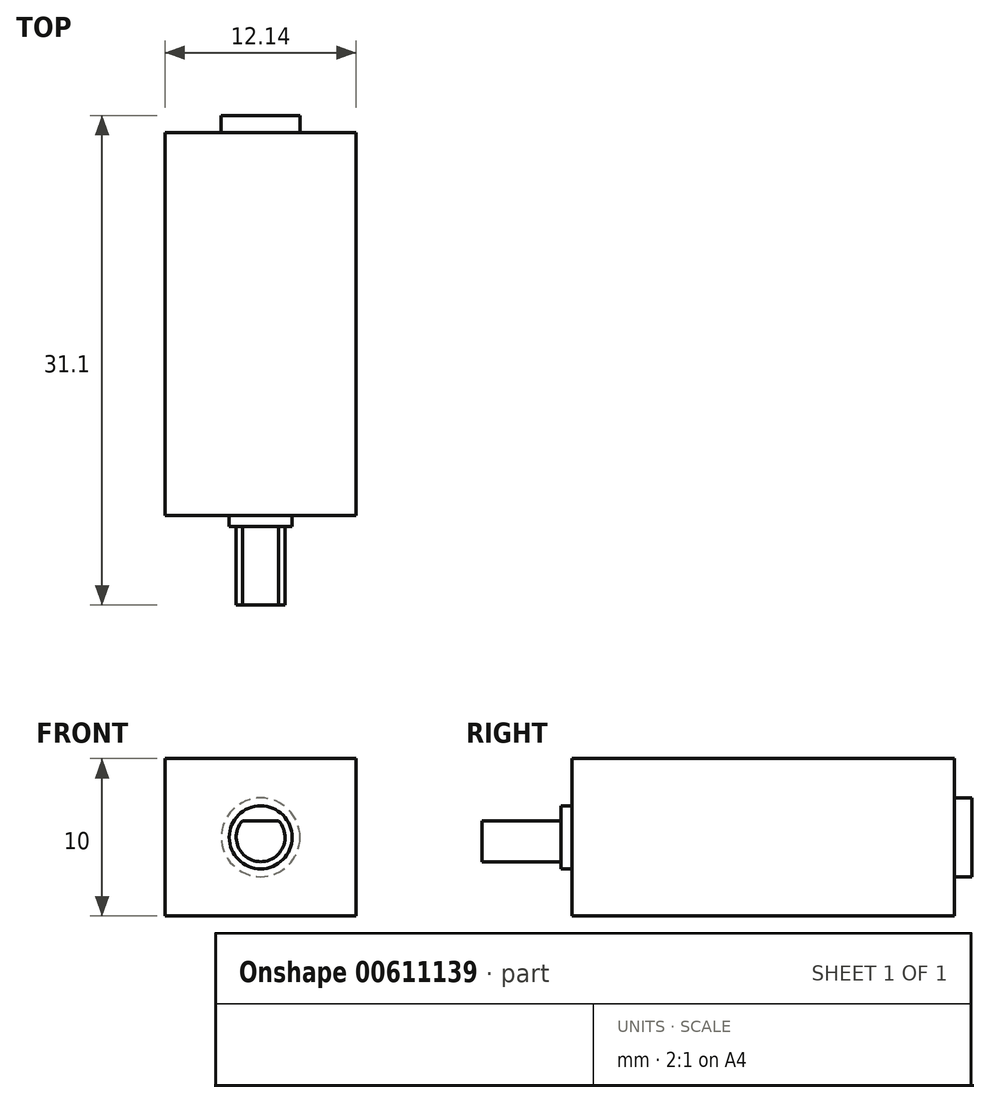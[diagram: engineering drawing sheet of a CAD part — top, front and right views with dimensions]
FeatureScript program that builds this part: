
annotation { "Feature Type Name" : "Feature", "Feature Type Description" : "" }
export const myFeature = defineFeature(function(context is Context, id is Id, definition is map)
    precondition{}
    {
        {
            var Q0;
            Q0=qCreatedBy(makeId("Top.planeOp"),FACE);
            var sketch = newSketch(context, id + "F0", { "sketchPlane" : qUnion([Q0])});
            skLineSegment(sketch, "E0.bottom", {"start": v(-55.86, 44.9) * mm, "end": v(-43.72, 44.9) * mm});
            skLineSegment(sketch, "E0.top", {"start": v(-55.86, 20.6) * mm, "end": v(-43.72, 20.6) * mm});
            skLineSegment(sketch, "E0.left", {"start": v(-55.86, 44.9) * mm, "end": v(-55.86, 20.6) * mm});
            skLineSegment(sketch, "E0.right", {"start": v(-43.72, 44.9) * mm, "end": v(-43.72, 20.6) * mm});
            skSolve(sketch);
        }
        {
            var Q0;
            Q0=makeQuery(id+"F0.imprint","IMPRINT",FACE,{"disambiguationData":[TD([[makeQuery(id+"F0.imprint","IMPRINT",EDGE,{"derivedFrom":sQuery(id+"F0.wireOp",EDGE,"E0.bottom")}),-1.0]])]});
            extrude(context, id + "F1", {"entities" : qUnion([Q0]), "depth" : 10 * mm, "offsetDistance" : 25 * mm});
        }
        {
            var Q0;
            Q0=makeQuery(id+"F1.opExtrude","SWEPT_FACE",FACE,{"disambiguationData":[OSD([sQuery(id+"F0.wireOp",EDGE,"E0.bottom")])]});
            var sketch = newSketch(context, id + "F2", { "sketchPlane" : qUnion([Q0])});
            skCircle(sketch, "E1", {"center": v(49.8, 5) * mm, "radius": 2.5 * mm});
            skSolve(sketch);
        }
        {
            var Q0;
            Q0=makeQuery(id+"F2.imprint","IMPRINT",FACE,{"disambiguationData":[TD([[makeQuery(id+"F2.imprint","IMPRINT",EDGE,{"derivedFrom":sQuery(id+"F2.wireOp",EDGE,"E1")}),1.0]])]});
            var Q1;
            Q1=sQuery(id+"F2.wireOp",EDGE,"E1");
            extrude(context, id + "F3", {"entities" : qUnion([Q0]), "operationType" : NewBodyOperationType.ADD, "surfaceEntities" : qUnion([Q1]), "depth" : 1.1 * mm, "offsetDistance" : 25 * mm});
        }
        {
            var Q0;
            Q0=makeQuery(id+"F1.opExtrude","SWEPT_FACE",FACE,{"disambiguationData":[OSD([sQuery(id+"F0.wireOp",EDGE,"E0.top")])]});
            var sketch = newSketch(context, id + "F4", { "sketchPlane" : qUnion([Q0])});
            skCircle(sketch, "E2", {"center": v(-49.8, 5) * mm, "radius": 2 * mm});
            skSolve(sketch);
        }
        {
            var Q0;
            Q0=makeQuery(id+"F4.imprint","IMPRINT",FACE,{"disambiguationData":[TD([[makeQuery(id+"F4.imprint","IMPRINT",EDGE,{"derivedFrom":sQuery(id+"F4.wireOp",EDGE,"E2")}),1.0]])]});
            var Q1;
            Q1=sQuery(id+"F4.wireOp",EDGE,"E2");
            extrude(context, id + "F5", {"entities" : qUnion([Q0]), "operationType" : NewBodyOperationType.ADD, "surfaceEntities" : qUnion([Q1]), "depth" : 0.7 * mm, "offsetDistance" : 25 * mm});
        }
        {
            var Q0;
            Q0=makeQuery(id+"F5.opExtrude","CAP_FACE",FACE,{"disambiguationData":[OSD([sQuery(id+"F4.wireOp",EDGE,"E2")])],"isStart":false});
            var sketch = newSketch(context, id + "F6", { "sketchPlane" : qUnion([Q0])});
            skCircle(sketch, "E3", {"center": v(-49.8, 5) * mm, "radius": 1.55 * mm});
            skLineSegment(sketch, "E4", {"start": v(-50.93, 6.05) * mm, "end": v(-48.65, 6.05) * mm});
            skSolve(sketch);
        }
        {
            var Q0;
            {var subQ0=sQuery(id+"F6.wireOp",EDGE,"E4");Q0=makeQuery(id+"F6.imprint","IMPRINT",FACE,{"disambiguationData":[TD([[makeQuery(id+"F6.imprint","IMPRINT",EDGE,{"derivedFrom":subQ0}),-1.0]])]});}
            extrude(context, id + "F7", {"entities" : qUnion([Q0]), "operationType" : NewBodyOperationType.ADD, "depth" : 5 * mm, "offsetDistance" : 25 * mm});
        }
        {
            var Q0;
            Q0=makeQuery(id+"F1.opExtrude","SWEPT_BODY",BODY,{"disambiguationData":[OSD([sQuery(id+"F0.wireOp",EDGE,"E0.bottom"),sQuery(id+"F0.wireOp",EDGE,"E0.top"),sQuery(id+"F0.wireOp",EDGE,"E0.left"),sQuery(id+"F0.wireOp",EDGE,"E0.right")])]});
            transform(context, id + "F8", {"entities" : qUnion([Q0]), "transformType" : TransformType.TRANSLATION_3D, "dx" : 20 * mm, "dy" : 0 * mm, "dz" : 0 * mm, "makeCopy" : true});
        }
        {
            var Q0;
            Q0=makeQuery(id+"F8.opPattern","COPY",BODY,{"derivedFrom":makeQuery(id+"F1.opExtrude","SWEPT_BODY",BODY,{"disambiguationData":[OSD([sQuery(id+"F0.wireOp",EDGE,"E0.bottom"),sQuery(id+"F0.wireOp",EDGE,"E0.top"),sQuery(id+"F0.wireOp",EDGE,"E0.left"),sQuery(id+"F0.wireOp",EDGE,"E0.right")])]}),"instanceName":"1"});
            deleteBodies(context, id + "F9", {"entities" : qUnion([Q0])});
        }
    });
